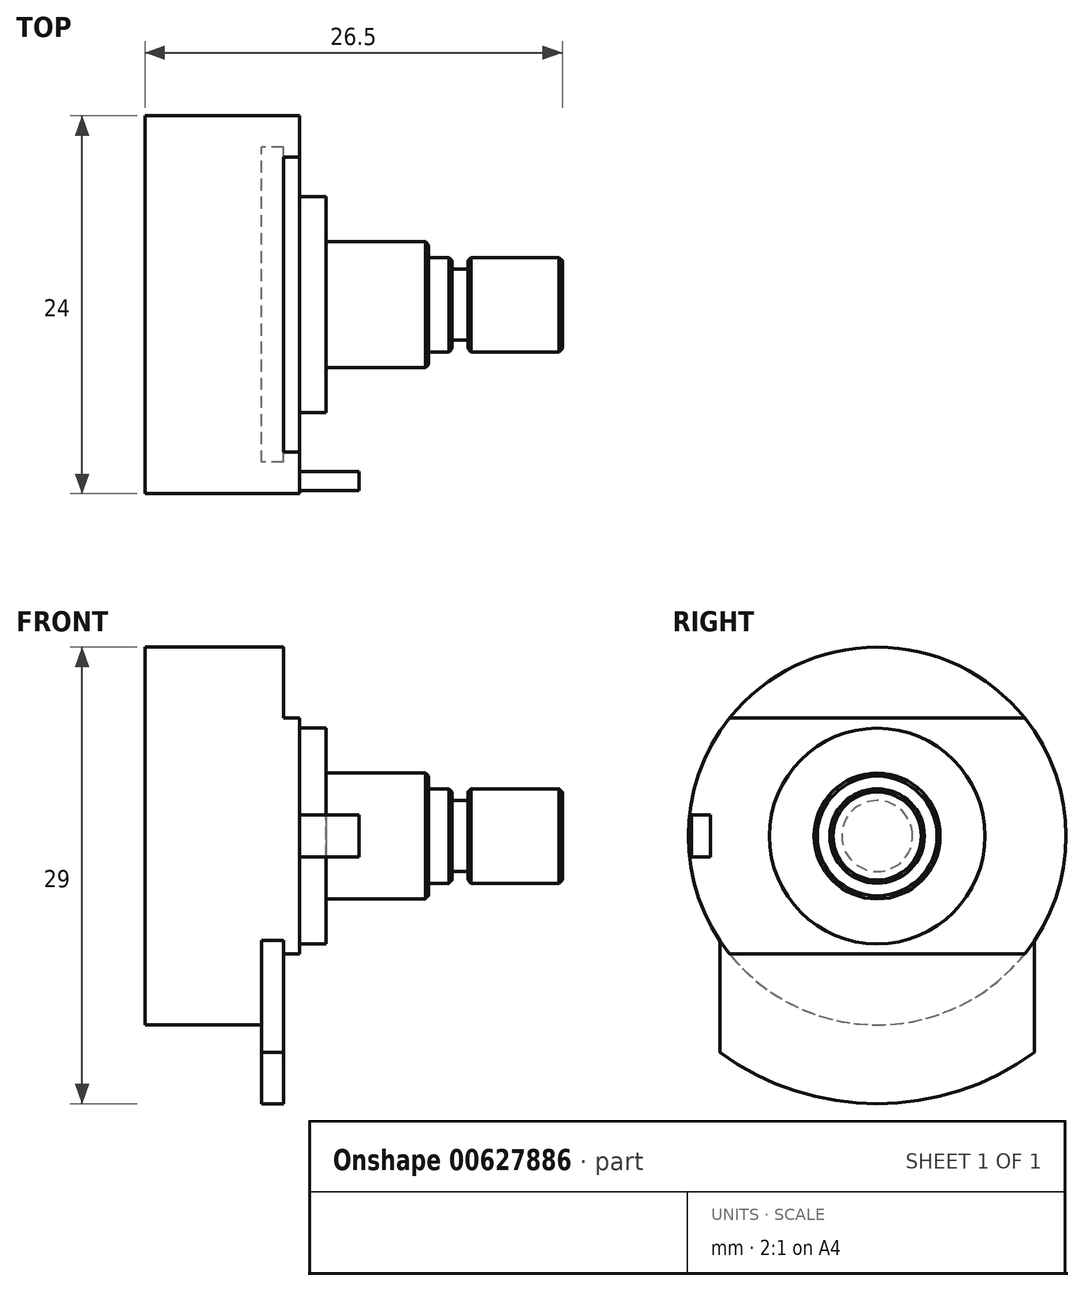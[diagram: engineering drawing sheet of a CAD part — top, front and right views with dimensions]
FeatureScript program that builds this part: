
annotation { "Feature Type Name" : "Feature", "Feature Type Description" : "" }
export const myFeature = defineFeature(function(context is Context, id is Id, definition is map)
    precondition{}
    {
        {
            var Q0;
            Q0=qCreatedBy(makeId("Front.planeOp"),FACE);
            var sketch = newSketch(context, id + "F0", { "sketchPlane" : qUnion([Q0])});
            skLineSegment(sketch, "E0", {"start": v(0, 0) * mm, "end": v(116.55, 0) * mm, "construction": true});
            skLineSegment(sketch, "E1", {"start": v(0, 0) * mm, "end": v(0, 12) * mm});
            skLineSegment(sketch, "E2", {"start": v(0, 12) * mm, "end": v(9.8, 12) * mm});
            skLineSegment(sketch, "E3", {"start": v(11.5, 6.85) * mm, "end": v(11.5, 0) * mm});
            skLineSegment(sketch, "E4", {"start": v(11.5, 0) * mm, "end": v(0, 0) * mm});
            skLineSegment(sketch, "E5", {"start": v(9.8, 12) * mm, "end": v(9.8, 6.85) * mm});
            skLineSegment(sketch, "E6", {"start": v(9.8, 6.85) * mm, "end": v(11.5, 6.85) * mm});
            skSolve(sketch);
        }
        {
            var Q0;
            Q0 = qSketchRegion(id + "F0", true);
            var Q1;
            Q1=sQuery(id+"F0.wireOp",EDGE,"E0");
            revolve(context, id + "F1", {"surfaceOperationType" : NewSurfaceOperationType.NEW, "entities" : qUnion([Q0]), "axis" : qUnion([Q1]), "revolveType" : RevolveType.FULL});
        }
        {
            var Q0;
            Q0=qCreatedBy(makeId("Front.planeOp"),FACE);
            var sketch = newSketch(context, id + "F2", { "sketchPlane" : qUnion([Q0])});
            skLineSegment(sketch, "E7", {"start": v(0, 0) * mm, "end": v(53.29, 0) * mm, "construction": true});
            skLineSegment(sketch, "E8.0", {"start": v(11.5, -11.87) * mm, "end": v(11.5, 12.13) * mm, "construction": true});
            skLineSegment(sketch, "E9.bottom", {"start": v(11.5, 4) * mm, "end": v(18, 4) * mm});
            skLineSegment(sketch, "E9.top", {"start": v(11.5, 0) * mm, "end": v(18, 0) * mm});
            skLineSegment(sketch, "E9.left", {"start": v(11.5, 4) * mm, "end": v(11.5, 0) * mm});
            skLineSegment(sketch, "E9.right", {"start": v(18, 4) * mm, "end": v(18, 0) * mm});
            skSolve(sketch);
        }
        {
            var Q0;
            Q0=makeQuery(id+"F2.imprint","IMPRINT",FACE,{"disambiguationData":[TD([[makeQuery(id+"F2.imprint","IMPRINT",EDGE,{"derivedFrom":sQuery(id+"F2.wireOp",EDGE,"E9.bottom")}),-1.0]])]});
            var Q1;
            Q1=sQuery(id+"F2.wireOp",EDGE,"E7");
            revolve(context, id + "F3", {"operationType" : NewBodyOperationType.ADD, "surfaceOperationType" : NewSurfaceOperationType.NEW, "entities" : qUnion([Q0]), "axis" : qUnion([Q1]), "revolveType" : RevolveType.FULL});
        }
        {
            var Q0;
            Q0=qCreatedBy(makeId("Front.planeOp"),FACE);
            var sketch = newSketch(context, id + "F4", { "sketchPlane" : qUnion([Q0])});
            skLineSegment(sketch, "E10", {"start": v(0, 0) * mm, "end": v(46.51, 0) * mm, "construction": true});
            skLineSegment(sketch, "E11.bottom", {"start": v(26.5, 0) * mm, "end": v(20.5, 0) * mm});
            skLineSegment(sketch, "E11.top", {"start": v(26.5, 3) * mm, "end": v(20.5, 3) * mm});
            skLineSegment(sketch, "E11.left", {"start": v(26.5, 0) * mm, "end": v(26.5, 3) * mm});
            skLineSegment(sketch, "E11.right", {"start": v(20.5, 0) * mm, "end": v(20.5, 3) * mm});
            skLineSegment(sketch, "E12.0", {"start": v(18, -4) * mm, "end": v(18, 4) * mm, "construction": true});
            skLineSegment(sketch, "E13", {"start": v(18, 0) * mm, "end": v(18, 3) * mm});
            skLineSegment(sketch, "E14", {"start": v(18, 3) * mm, "end": v(19.5, 3) * mm});
            skLineSegment(sketch, "E15", {"start": v(19.5, 3) * mm, "end": v(19.5, 0) * mm});
            skLineSegment(sketch, "E16", {"start": v(19.5, 0) * mm, "end": v(18, 0) * mm});
            skLineSegment(sketch, "E17", {"start": v(19.5, 2.25) * mm, "end": v(20.5, 2.25) * mm});
            skLineSegment(sketch, "E18", {"start": v(19.5, 0) * mm, "end": v(20.5, 0) * mm});
            skSolve(sketch);
        }
        {
            var Q0;
            Q0 = qSketchRegion(id + "F4", true);
            var Q1;
            Q1=sQuery(id+"F4.wireOp",EDGE,"E10");
            revolve(context, id + "F5", {"operationType" : NewBodyOperationType.ADD, "surfaceOperationType" : NewSurfaceOperationType.NEW, "entities" : qUnion([Q0]), "axis" : qUnion([Q1]), "revolveType" : RevolveType.FULL});
        }
        {
            var Q0;
            Q0=makeQuery(id+"F3.opRevolve","SWEPT_EDGE",EDGE,{"disambiguationData":[OSD([sQuery(id+"F2.wireOp",EDGE,"E9.bottom"),sQuery(id+"F2.wireOp",EDGE,"E9.right")])]});
            var Q1;
            Q1=makeQuery(id+"F5.opRevolve","SWEPT_EDGE",EDGE,{"disambiguationData":[OSD([sQuery(id+"F4.wireOp",EDGE,"E14"),sQuery(id+"F4.wireOp",EDGE,"E15")])]});
            var Q2;
            Q2=makeQuery(id+"F5.opRevolve","SWEPT_EDGE",EDGE,{"disambiguationData":[OSD([sQuery(id+"F4.wireOp",EDGE,"E11.top"),sQuery(id+"F4.wireOp",EDGE,"E11.right")])]});
            var Q3;
            Q3=makeQuery(id+"F5.opRevolve","SWEPT_EDGE",EDGE,{"disambiguationData":[OSD([sQuery(id+"F4.wireOp",EDGE,"E11.top"),sQuery(id+"F4.wireOp",EDGE,"E11.left")])]});
            chamfer(context, id + "F6", {"entities" : qUnion([Q0, Q1, Q2, Q3]), "width" : .2 * mm, "tangentPropagation" : true});
        }
        {
            var Q0;
            Q0=makeQuery(id+"F1.opRevolve","SWEPT_FACE",FACE,{"disambiguationData":[OSD([sQuery(id+"F0.wireOp",EDGE,"E5")])]});
            var sketch = newSketch(context, id + "F7", { "sketchPlane" : qUnion([Q0])});
            skLineSegment(sketch, "E19", {"start": v(0, 0) * mm, "end": v(22.75, 0) * mm, "construction": true});
            skLineSegment(sketch, "E20.bottom", {"start": v(-17.5, 7.5) * mm, "end": v(17.5, 7.5) * mm});
            skLineSegment(sketch, "E20.top", {"start": v(-17.5, 14.5) * mm, "end": v(17.5, 14.5) * mm});
            skLineSegment(sketch, "E20.left", {"start": v(-17.5, 7.5) * mm, "end": v(-17.5, 14.5) * mm});
            skLineSegment(sketch, "E20.right", {"start": v(17.5, 7.5) * mm, "end": v(17.5, 14.5) * mm});
            skLineSegment(sketch, "E21.MirrorCS", {"start": v(-17.5, -7.5) * mm, "end": v(-17.5, -14.5) * mm});
            skLineSegment(sketch, "E22.MirrorCS", {"start": v(-17.5, -14.5) * mm, "end": v(17.5, -14.5) * mm});
            skLineSegment(sketch, "E23.MirrorCS", {"start": v(-17.5, -7.5) * mm, "end": v(17.5, -7.5) * mm});
            skLineSegment(sketch, "E24.MirrorCS", {"start": v(17.5, -7.5) * mm, "end": v(17.5, -14.5) * mm});
            skLineSegment(sketch, "E25", {"start": v(0, 0) * mm, "end": v(0, 14.5) * mm, "construction": true});
            skSolve(sketch);
        }
        {
            var Q0;
            Q0 = qSketchRegion(id + "F7", true);
            extrude(context, id + "F8", {"entities" : qUnion([Q0]), "operationType" : NewBodyOperationType.REMOVE, "oppositeDirection" : true, "depth" : 2.4 * mm, "offsetDistance" : 25 * mm});
        }
        {
            var Q0;
            Q0=makeQuery(id+"F8.boolean.opBoolean","COPY",FACE,{"derivedFrom":makeQuery(id+"F8.opExtrude","CAP_FACE",FACE,{"disambiguationData":[OSD([sQuery(id+"F7.wireOp",EDGE,"E20.bottom"),sQuery(id+"F7.wireOp",EDGE,"E20.top"),sQuery(id+"F7.wireOp",EDGE,"E20.left"),sQuery(id+"F7.wireOp",EDGE,"E20.right")])],"isStart":false})});
            var sketch = newSketch(context, id + "F9", { "sketchPlane" : qUnion([Q0])});
            skLineSegment(sketch, "E26", {"start": v(0, 0) * mm, "end": v(0, -28.6) * mm, "construction": true});
            skLineSegment(sketch, "E27", {"start": v(0, 0) * mm, "end": v(23.74, 0) * mm, "construction": true});
            skArc(sketch, "E28.0", {"start": v(-9.37, 7.5) * mm, "mid": v(0, 12) * mm, "end": v(9.37, 7.5) * mm});
            skArc(sketch, "E29.0", {"start": v(-9.37, -7.5) * mm, "mid": v(-12, 0) * mm, "end": v(-9.37, 7.5) * mm});
            skArc(sketch, "E30.0", {"start": v(9.37, 7.5) * mm, "mid": v(12, 0) * mm, "end": v(9.37, -7.5) * mm});
            skArc(sketch, "E31.0", {"start": v(9.37, -7.5) * mm, "mid": v(0, -12) * mm, "end": v(-9.37, -7.5) * mm});
            skArc(sketch, "E32", {"start": v(-10, -13.75) * mm, "mid": v(0, -17) * mm, "end": v(10, -13.75) * mm});
            skLineSegment(sketch, "E33", {"start": v(-10, -6.63) * mm, "end": v(-10, -13.75) * mm});
            skLineSegment(sketch, "E34.MirrorCS", {"start": v(10, -6.63) * mm, "end": v(10, -13.75) * mm});
            skLineSegment(sketch, "E35", {"start": v(0, -17) * mm, "end": v(18.07, -17) * mm, "construction": true});
            skLineSegment(sketch, "E36", {"start": v(0, 12) * mm, "end": v(13.12, 12) * mm, "construction": true});
            skSolve(sketch);
        }
        {
            var Q0;
            Q0 = qSketchRegion(id + "F9", true);
            extrude(context, id + "F10", {"entities" : qUnion([Q0]), "operationType" : NewBodyOperationType.ADD, "depth" : 1.4 * mm, "offsetDistance" : 25 * mm});
        }
        {
            var Q0;
            Q0=makeQuery(id+"F1.opRevolve","SWEPT_FACE",FACE,{"disambiguationData":[OSD([sQuery(id+"F0.wireOp",EDGE,"E5")])]});
            var sketch = newSketch(context, id + "F11", { "sketchPlane" : qUnion([Q0])});
            skLineSegment(sketch, "E37", {"start": v(0, 0) * mm, "end": v(-11.8, 0) * mm, "construction": true});
            skLineSegment(sketch, "E38", {"start": v(0, 0) * mm, "end": v(0, 7.05) * mm, "construction": true});
            skLineSegment(sketch, "E39.bottom", {"start": v(-11.8, 1.32) * mm, "end": v(-10.6, 1.32) * mm});
            skLineSegment(sketch, "E39.top", {"start": v(-11.8, -1.33) * mm, "end": v(-10.6, -1.33) * mm});
            skLineSegment(sketch, "E39.left", {"start": v(-11.8, 1.32) * mm, "end": v(-11.8, -1.33) * mm});
            skLineSegment(sketch, "E39.right", {"start": v(-10.6, 1.33) * mm, "end": v(-10.6, -1.33) * mm});
            skLineSegment(sketch, "E40", {"start": v(-11.2, 1.32) * mm, "end": v(-11.2, -1.33) * mm, "construction": true});
            skSolve(sketch);
        }
        {
            var Q0;
            Q0 = qSketchRegion(id + "F11", true);
            extrude(context, id + "F12", {"entities" : qUnion([Q0]), "operationType" : NewBodyOperationType.ADD, "depth" : 3.8 * mm, "offsetDistance" : 25 * mm});
        }
    });
